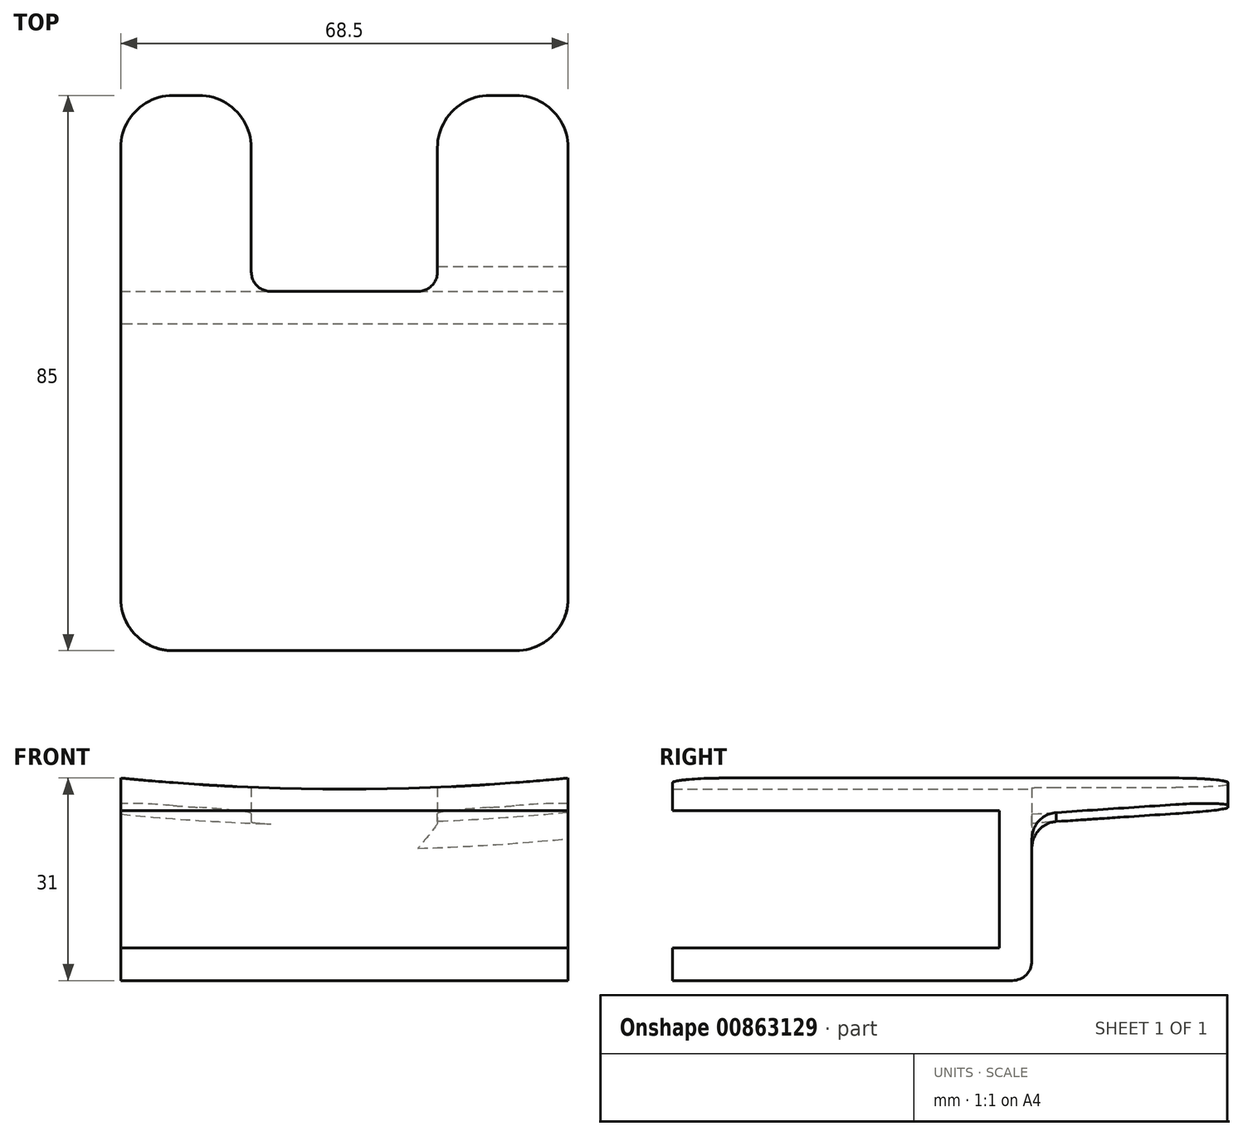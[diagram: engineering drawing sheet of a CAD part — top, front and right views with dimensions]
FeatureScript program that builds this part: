
annotation { "Feature Type Name" : "Feature", "Feature Type Description" : "" }
export const myFeature = defineFeature(function(context is Context, id is Id, definition is map)
    precondition{}
    {
        {
            var Q0;
            Q0=qCreatedBy(makeId("Top.planeOp"),FACE);
            var sketch = newSketch(context, id + "F0", { "sketchPlane" : qUnion([Q0])});
            skLineSegment(sketch, "E0", {"start": v(-34.25, 22) * mm, "end": v(-34.25, -47) * mm});
            skLineSegment(sketch, "E1", {"start": v(-26.25, -55) * mm, "end": v(26.25, -55) * mm});
            skLineSegment(sketch, "E2", {"start": v(34.25, -47) * mm, "end": v(34.25, 22) * mm});
            skLineSegment(sketch, "E3", {"start": v(26.25, 30) * mm, "end": v(22.25, 30) * mm});
            skLineSegment(sketch, "E4", {"start": v(14.25, 22) * mm, "end": v(14.25, 3) * mm});
            skLineSegment(sketch, "E5", {"start": v(11.25, 0) * mm, "end": v(-11.25, 0) * mm});
            skLineSegment(sketch, "E6", {"start": v(-14.25, 3) * mm, "end": v(-14.25, 22) * mm});
            skLineSegment(sketch, "E7", {"start": v(-22.25, 30) * mm, "end": v(-26.25, 30) * mm});
            skPoint(sketch, "E8.visualSharp", {"position": v(-34.25, -55) * mm});
            skArc(sketch, "E8.filletArc", {"start": v(-34.25, -47) * mm, "mid": v(-31.9, -52.66) * mm, "end": v(-26.25, -55) * mm});
            skPoint(sketch, "E9.visualSharp", {"position": v(34.25, -55) * mm});
            skArc(sketch, "E9.filletArc", {"start": v(26.25, -55) * mm, "mid": v(31.9, -52.66) * mm, "end": v(34.25, -47) * mm});
            skPoint(sketch, "E10.visualSharp", {"position": v(-34.25, 30) * mm});
            skArc(sketch, "E10.filletArc", {"start": v(-26.25, 30) * mm, "mid": v(-31.9, 27.66) * mm, "end": v(-34.25, 22) * mm});
            skPoint(sketch, "E11.visualSharp", {"position": v(-14.25, 30) * mm});
            skArc(sketch, "E11.filletArc", {"start": v(-14.25, 22) * mm, "mid": v(-16.6, 27.66) * mm, "end": v(-22.25, 30) * mm});
            skPoint(sketch, "E12.visualSharp", {"position": v(14.25, 30) * mm});
            skArc(sketch, "E12.filletArc", {"start": v(22.25, 30) * mm, "mid": v(16.6, 27.66) * mm, "end": v(14.25, 22) * mm});
            skPoint(sketch, "E13.visualSharp", {"position": v(34.25, 30) * mm});
            skArc(sketch, "E13.filletArc", {"start": v(34.25, 22) * mm, "mid": v(31.9, 27.66) * mm, "end": v(26.25, 30) * mm});
            skPoint(sketch, "E14.visualSharp", {"position": v(-14.25, 0) * mm});
            skArc(sketch, "E14.filletArc", {"start": v(-14.25, 3) * mm, "mid": v(-13.37, 0.88) * mm, "end": v(-11.25, 0) * mm});
            skPoint(sketch, "E15.visualSharp", {"position": v(14.25, 0) * mm});
            skArc(sketch, "E15.filletArc", {"start": v(11.25, 0) * mm, "mid": v(13.37, 0.88) * mm, "end": v(14.25, 3) * mm});
            skSolve(sketch);
        }
        {
            var Q0;
            Q0=qSketchRegion(id+"F0",true);
            extrude(context, id + "F1", {"entities" : qUnion([Q0]), "depth" : 10 * mm, "offsetDistance" : 25 * mm});
        }
        {
            var Q0;
            Q0=qCreatedBy(makeId("Front.planeOp"),FACE);
            var sketch = newSketch(context, id + "F2", { "sketchPlane" : qUnion([Q0])});
            skPoint(sketch, "E16", {"position": v(0, 8.3) * mm});
            skPoint(sketch, "E17", {"position": v(-34.25, 10) * mm});
            skPoint(sketch, "E18", {"position": v(34.25, 10) * mm});
            skArc(sketch, "E19", {"start": v(-34.25, 10) * mm, "mid": v(0, 8.3) * mm, "end": v(34.25, 10) * mm});
            skArc(sketch, "E20", {"start": v(34.25, 10) * mm, "mid": v(0, 24.37) * mm, "end": v(-34.25, 10) * mm});
            skSolve(sketch);
        }
        {
            var Q0;
            Q0 = qSketchRegion(id + "F2", true);
            extrude(context, id + "F3", {"entities" : qUnion([Q0]), "operationType" : NewBodyOperationType.REMOVE, "endBound" : BoundingType.SYMMETRIC, "depth" : 150 * mm, "offsetDistance" : 25 * mm});
        }
        {
            var Q0;
            Q0=qCreatedBy(makeId("Front.planeOp"),FACE);
            var sketch = newSketch(context, id + "F4", { "sketchPlane" : qUnion([Q0])});
            skLineSegment(sketch, "E21", {"start": v(-34.25, 4.47) * mm, "end": v(-34.25, -5.08) * mm});
            skLineSegment(sketch, "E22", {"start": v(34.25, -5.08) * mm, "end": v(-34.25, -5.08) * mm});
            skLineSegment(sketch, "E23", {"start": v(34.25, -5.08) * mm, "end": v(34.25, 4.47) * mm});
            skArc(sketch, "E24.0", {"start": v(-34.25, 4.47) * mm, "mid": v(0, 2.8) * mm, "end": v(34.25, 4.47) * mm});
            skSolve(sketch);
        }
        {
            var Q0;
            Q0=makeQuery(id+"F1.opExtrude","SWEPT_FACE",FACE,{"disambiguationData":[OSD([sQuery(id+"F0.wireOp",EDGE,"E7")])]});
            var sketch = newSketch(context, id + "F5", { "sketchPlane" : qUnion([Q0])});
            skArc(sketch, "E25.0", {"start": v(34.25, 6.48) * mm, "mid": v(0, 4.8) * mm, "end": v(-34.25, 6.48) * mm});
            skLineSegment(sketch, "E26", {"start": v(-34.25, 6.48) * mm, "end": v(-34.25, -5.08) * mm});
            skLineSegment(sketch, "E27", {"start": v(-34.25, -5.08) * mm, "end": v(34.25, -5.08) * mm});
            skLineSegment(sketch, "E28", {"start": v(34.25, -5.08) * mm, "end": v(34.25, 6.48) * mm});
            skSolve(sketch);
        }
        {
            var Q1;
            Q1 = qSketchRegion(id + "F4", true);
            var Q2;
            Q2 = qSketchRegion(id + "F5", true);
            loft(context, id + "F6", {"operationType" : NewBodyOperationType.REMOVE, "sheetProfilesArray" : [{ "sheetProfileEntities" : qUnion([Q1]) }, { "sheetProfileEntities" : qUnion([Q2]) }]});
        }
        {
            var Q0;
            Q0=makeQuery(id+"F1.opExtrude","SWEPT_FACE",FACE,{"disambiguationData":[OSD([sQuery(id+"F0.wireOp",EDGE,"E0")])]});
            var sketch = newSketch(context, id + "F7", { "sketchPlane" : qUnion([Q0])});
            skLineSegment(sketch, "E29", {"start": v(55, -3) * mm, "end": v(0, -3) * mm});
            skLineSegment(sketch, "E30", {"start": v(0, 5) * mm, "end": v(55, 5) * mm});
            skLineSegment(sketch, "E31", {"start": v(55, -3) * mm, "end": v(55, 5) * mm});
            skLineSegment(sketch, "E32", {"start": v(0, 0) * mm, "end": v(0, 0) * mm});
            skLineSegment(sketch, "E33", {"start": v(0, -3) * mm, "end": v(0, 5) * mm});
            skSolve(sketch);
        }
        {
            var Q0;
            Q0=qSketchRegion(id+"F7",true);
            extrude(context, id + "F8", {"entities" : qUnion([Q0]), "operationType" : NewBodyOperationType.REMOVE, "endBound" : BoundingType.THROUGH_ALL, "oppositeDirection" : true, "depth" : 25 * mm, "offsetDistance" : 25 * mm});
        }
        {
            var Q0;
            Q0=makeQuery(id+"F8.boolean.opBoolean","COPY",FACE,{"derivedFrom":makeQuery(id+"F8.opExtrude","SWEPT_FACE",FACE,{"disambiguationData":[OSD([sQuery(id+"F7.wireOp",EDGE,"E30")])]})});
            var sketch = newSketch(context, id + "F9", { "sketchPlane" : qUnion([Q0])});
            skLineSegment(sketch, "E34.bottom", {"start": v(34.25, 0) * mm, "end": v(-34.25, 0) * mm});
            skLineSegment(sketch, "E34.top", {"start": v(34.25, 5) * mm, "end": v(-34.25, 5) * mm});
            skLineSegment(sketch, "E34.left", {"start": v(34.25, 0) * mm, "end": v(34.25, 5) * mm});
            skLineSegment(sketch, "E34.right", {"start": v(-34.25, 0) * mm, "end": v(-34.25, 5) * mm});
            skSolve(sketch);
        }
        {
            var Q0;
            Q0=qSketchRegion(id+"F9",true);
            extrude(context, id + "F10", {"entities" : qUnion([Q0]), "operationType" : NewBodyOperationType.ADD, "depth" : 21 * mm, "offsetDistance" : 25 * mm});
        }
        {
            var Q0;
            Q0=makeQuery(id+"F6.boolean.opBoolean","COPY",EDGE,{"derivedFrom":makeQuery(id+"F6.opLoft","MID_CAP_EDGE",EDGE,{"disambiguationData":[OSD([sQuery(id+"F4.wireOp",EDGE,"E21"),sQuery(id+"F4.wireOp",EDGE,"E24.0"),sQuery(id+"F5.wireOp",EDGE,"E25.0"),sQuery(id+"F5.wireOp",EDGE,"E28")])],"capPos":0.0})});
            var Q1;
            Q1=makeQuery(id+"F6.boolean.opBoolean","COPY",EDGE,{"derivedFrom":makeQuery(id+"F6.opLoft","MID_CAP_EDGE",EDGE,{"disambiguationData":[OSD([sQuery(id+"F0.wireOp",EDGE,"E7"),sQuery(id+"F0.wireOp",EDGE,"E10.filletArc"),sQuery(id+"F4.wireOp",EDGE,"E23"),sQuery(id+"F4.wireOp",EDGE,"E24.0"),sQuery(id+"F5.wireOp",EDGE,"E25.0")])],"capPos":0.0})});
            fillet(context, id + "F11", {"entities" : qUnion([Q0, Q1]), "radius" : 4 * mm, "tangentPropagation" : true, "allowEdgeOverflow" : false});
        }
        {
            var Q0;
            Q0=makeQuery(id+"F10.opExtrude","CAP_FACE",FACE,{"disambiguationData":[OSD([sQuery(id+"F9.wireOp",EDGE,"E34.bottom"),sQuery(id+"F9.wireOp",EDGE,"E34.top"),sQuery(id+"F9.wireOp",EDGE,"E34.left"),sQuery(id+"F9.wireOp",EDGE,"E34.right")])],"isStart":false});
            var sketch = newSketch(context, id + "F12", { "sketchPlane" : qUnion([Q0])});
            skLineSegment(sketch, "E35", {"start": v(34.25, 0) * mm, "end": v(-34.25, 0) * mm});
            skLineSegment(sketch, "E36", {"start": v(-34.25, 0) * mm, "end": v(-34.25, 47) * mm});
            skLineSegment(sketch, "E37", {"start": v(-26.25, 55) * mm, "end": v(26.25, 55) * mm});
            skLineSegment(sketch, "E38", {"start": v(34.25, 47) * mm, "end": v(34.25, 0) * mm});
            skPoint(sketch, "E39.visualSharp", {"position": v(-34.25, 55) * mm});
            skArc(sketch, "E39.filletArc", {"start": v(-26.25, 55) * mm, "mid": v(-31.9, 52.66) * mm, "end": v(-34.25, 47) * mm});
            skPoint(sketch, "E40.visualSharp", {"position": v(34.25, 55) * mm});
            skArc(sketch, "E40.filletArc", {"start": v(34.25, 47) * mm, "mid": v(31.9, 52.66) * mm, "end": v(26.25, 55) * mm});
            skSolve(sketch);
        }
        {
            var Q0;
            Q0=qSketchRegion(id+"F12",true);
            extrude(context, id + "F13", {"entities" : qUnion([Q0]), "operationType" : NewBodyOperationType.ADD, "depth" : 5 * mm, "offsetDistance" : 25 * mm});
        }
        {
            var Q0;
            Q0=makeQuery(id+"F13.opExtrude","CAP_EDGE",EDGE,{"disambiguationData":[OSD([sQuery(id+"F12.wireOp",EDGE,"E35")])],"isStart":false});
            var Q1;
            Q1=makeQuery(id+"F10.opExtrude","CAP_EDGE",EDGE,{"disambiguationData":[OSD([sQuery(id+"F9.wireOp",EDGE,"E34.top")])],"isStart":false});
            var Q2;
            Q2=makeQuery(id+"F10.opExtrude","CAP_EDGE",EDGE,{"disambiguationData":[OSD([sQuery(id+"F9.wireOp",EDGE,"E34.top")])],"isStart":true});
            fillet(context, id + "F14", {"entities" : qUnion([Q0, Q1, Q2]), "radius" : 3 * mm, "tangentPropagation" : true, "allowEdgeOverflow" : false});
        }
    });
